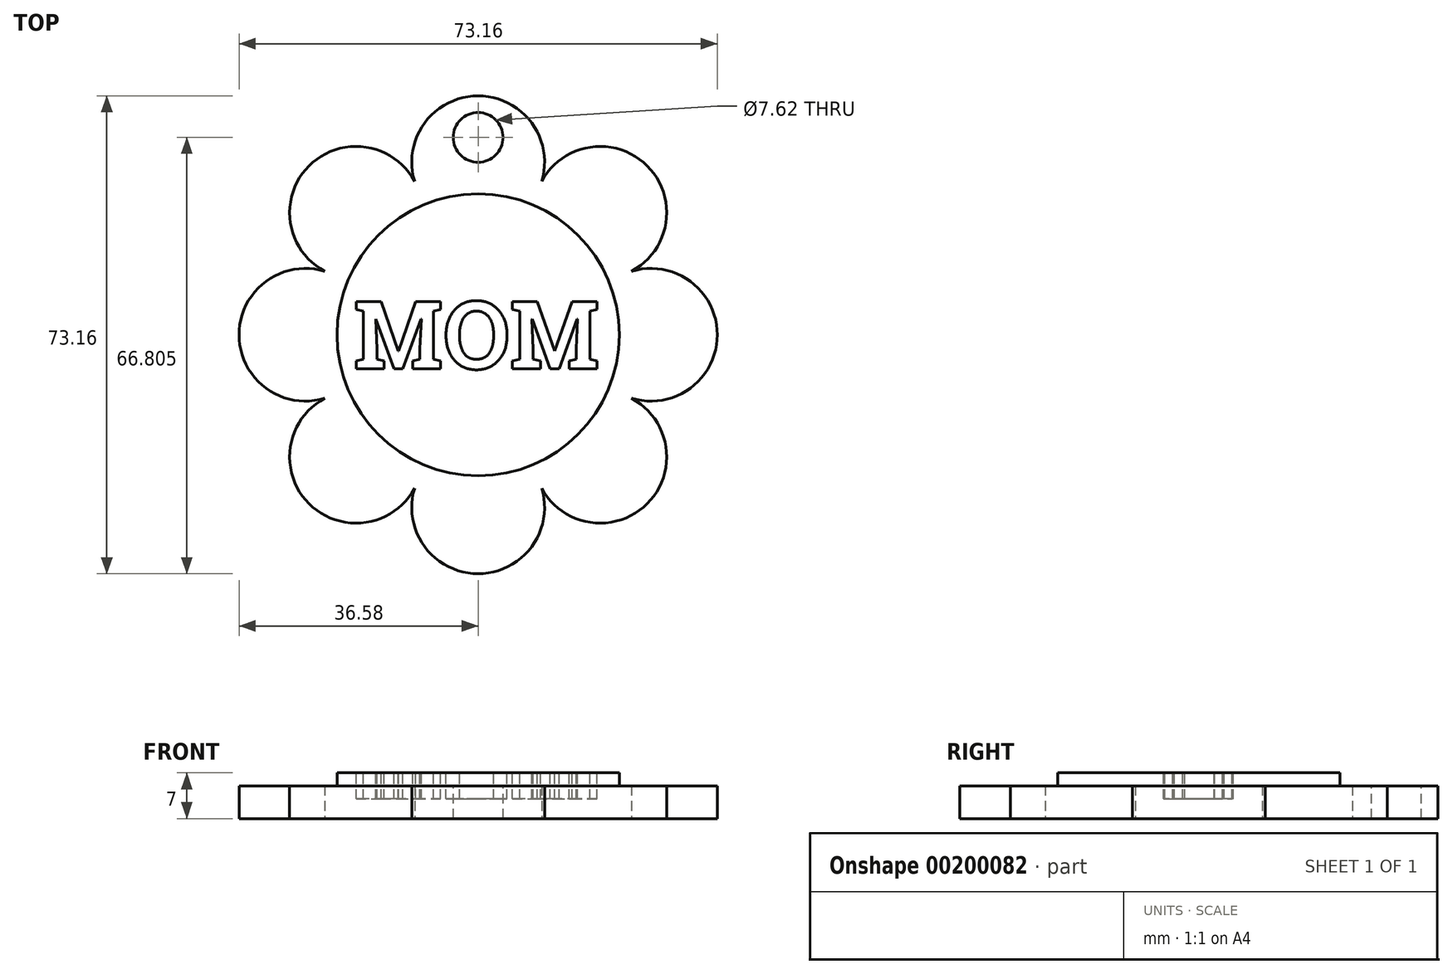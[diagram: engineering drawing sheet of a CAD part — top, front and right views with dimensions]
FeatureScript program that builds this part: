
annotation { "Feature Type Name" : "Feature", "Feature Type Description" : "" }
export const myFeature = defineFeature(function(context is Context, id is Id, definition is map)
    precondition{}
    {
        {
            var Q0;
            Q0=qCreatedBy(makeId("Top.planeOp"),FACE);
            var sketch = newSketch(context, id + "F0", { "sketchPlane" : qUnion([Q0])});
            skCircle(sketch, "E0.cCircle", {"center": v(0, 0) * mm, "radius": 23.47 * mm, "construction": true});
            skLineSegment(sketch, "E0.0", {"start": v(-9.72, 23.47) * mm, "end": v(9.72, 23.47) * mm});
            skLineSegment(sketch, "E0.1", {"start": v(9.72, 23.47) * mm, "end": v(23.47, 9.72) * mm});
            skLineSegment(sketch, "E0.2", {"start": v(23.47, 9.72) * mm, "end": v(23.47, -9.72) * mm});
            skLineSegment(sketch, "E0.3", {"start": v(23.47, -9.72) * mm, "end": v(9.72, -23.47) * mm});
            skLineSegment(sketch, "E0.4", {"start": v(9.72, -23.47) * mm, "end": v(-9.72, -23.47) * mm});
            skLineSegment(sketch, "E0.5", {"start": v(-9.72, -23.47) * mm, "end": v(-23.47, -9.72) * mm});
            skLineSegment(sketch, "E0.6", {"start": v(-23.47, -9.72) * mm, "end": v(-23.47, 9.72) * mm});
            skLineSegment(sketch, "E0.7", {"start": v(-23.47, 9.72) * mm, "end": v(-9.72, 23.47) * mm});
            skPoint(sketch, "E0.0.midPoint", {"position": v(0, 23.47) * mm});
            skArc(sketch, "E1", {"start": v(23.47, 9.72) * mm, "mid": v(25.87, 25.87) * mm, "end": v(9.72, 23.47) * mm});
            skArc(sketch, "E2", {"start": v(23.47, -9.72) * mm, "mid": v(36.58, 0) * mm, "end": v(23.47, 9.72) * mm});
            skArc(sketch, "E3", {"start": v(9.72, -23.47) * mm, "mid": v(25.87, -25.87) * mm, "end": v(23.47, -9.72) * mm});
            skArc(sketch, "E4", {"start": v(-9.72, -23.47) * mm, "mid": v(0, -36.58) * mm, "end": v(9.72, -23.47) * mm});
            skArc(sketch, "E5", {"start": v(-23.47, 9.72) * mm, "mid": v(-36.58, 0) * mm, "end": v(-23.47, -9.72) * mm});
            skArc(sketch, "E6", {"start": v(-9.72, 23.47) * mm, "mid": v(-25.87, 25.87) * mm, "end": v(-23.47, 9.72) * mm});
            skArc(sketch, "E7", {"start": v(9.72, 23.47) * mm, "mid": v(0, 36.58) * mm, "end": v(-9.72, 23.47) * mm});
            skArc(sketch, "E8", {"start": v(-23.47, -9.72) * mm, "mid": v(-25.87, -25.87) * mm, "end": v(-9.72, -23.47) * mm});
            skSolve(sketch);
        }
        {
            var Q0;
            Q0 = qSketchRegion(id + "F0", true);
            extrude(context, id + "F1", {"entities" : qUnion([Q0]), "depth" : 5 * mm});
        }
        {
            var Q0;
            Q0=makeQuery(id+"F1.opExtrude","CAP_FACE",FACE,{"disambiguationData":[OSD([sQuery(id+"F0.wireOp",EDGE,"E1"),sQuery(id+"F0.wireOp",EDGE,"E2"),sQuery(id+"F0.wireOp",EDGE,"E3"),sQuery(id+"F0.wireOp",EDGE,"E4"),sQuery(id+"F0.wireOp",EDGE,"E5"),sQuery(id+"F0.wireOp",EDGE,"E6"),sQuery(id+"F0.wireOp",EDGE,"E7"),sQuery(id+"F0.wireOp",EDGE,"E8")])],"isStart":false});
            var sketch = newSketch(context, id + "F2", { "sketchPlane" : qUnion([Q0])});
            skCircle(sketch, "E9", {"center": v(0, 0) * mm, "radius": 21.59 * mm});
            skSolve(sketch);
        }
        {
            var Q0;
            Q0 = qSketchRegion(id + "F2", true);
            extrude(context, id + "F3", {"entities" : qUnion([Q0]), "operationType" : NewBodyOperationType.ADD, "depth" : 2 * mm});
        }
        {
            var Q0;
            Q0=makeQuery(id+"F3.opExtrude","CAP_FACE",FACE,{"disambiguationData":[OSD([sQuery(id+"F2.wireOp",EDGE,"E9")])],"isStart":false});
            var sketch = newSketch(context, id + "F4", { "sketchPlane" : qUnion([Q0])});
            skText(sketch, "E10", { "text": "MOM", "fontName": "RobotoSlab-Bold.ttf"});
            const initialGuessF4  = {"E10": [-0.01905, -0.00522, 1, 0, 0.01044]};
            skSetInitialGuess(sketch, initialGuessF4);
            skSolve(sketch);
        }
        {
            var Q0;
            Q0 = qSketchRegion(id + "F4", true);
            extrude(context, id + "F5", {"entities" : qUnion([Q0]), "operationType" : NewBodyOperationType.REMOVE, "oppositeDirection" : true, "depth" : 4 * mm});
        }
        {
            var Q0;
            Q0=makeQuery(id+"F1.opExtrude","CAP_FACE",FACE,{"disambiguationData":[OSD([sQuery(id+"F0.wireOp",EDGE,"E1"),sQuery(id+"F0.wireOp",EDGE,"E2"),sQuery(id+"F0.wireOp",EDGE,"E3"),sQuery(id+"F0.wireOp",EDGE,"E4"),sQuery(id+"F0.wireOp",EDGE,"E5"),sQuery(id+"F0.wireOp",EDGE,"E6"),sQuery(id+"F0.wireOp",EDGE,"E7"),sQuery(id+"F0.wireOp",EDGE,"E8")])],"isStart":false});
            var sketch = newSketch(context, id + "F6", { "sketchPlane" : qUnion([Q0])});
            skCircle(sketch, "E11", {"center": v(0, 30.23) * mm, "radius": 3.81 * mm});
            skSolve(sketch);
        }
        {
            var Q0;
            Q0 = qSketchRegion(id + "F6", true);
            extrude(context, id + "F7", {"entities" : qUnion([Q0]), "operationType" : NewBodyOperationType.REMOVE, "endBound" : BoundingType.THROUGH_ALL, "oppositeDirection" : true, "depth" : 25.4 * mm});
        }
    });
